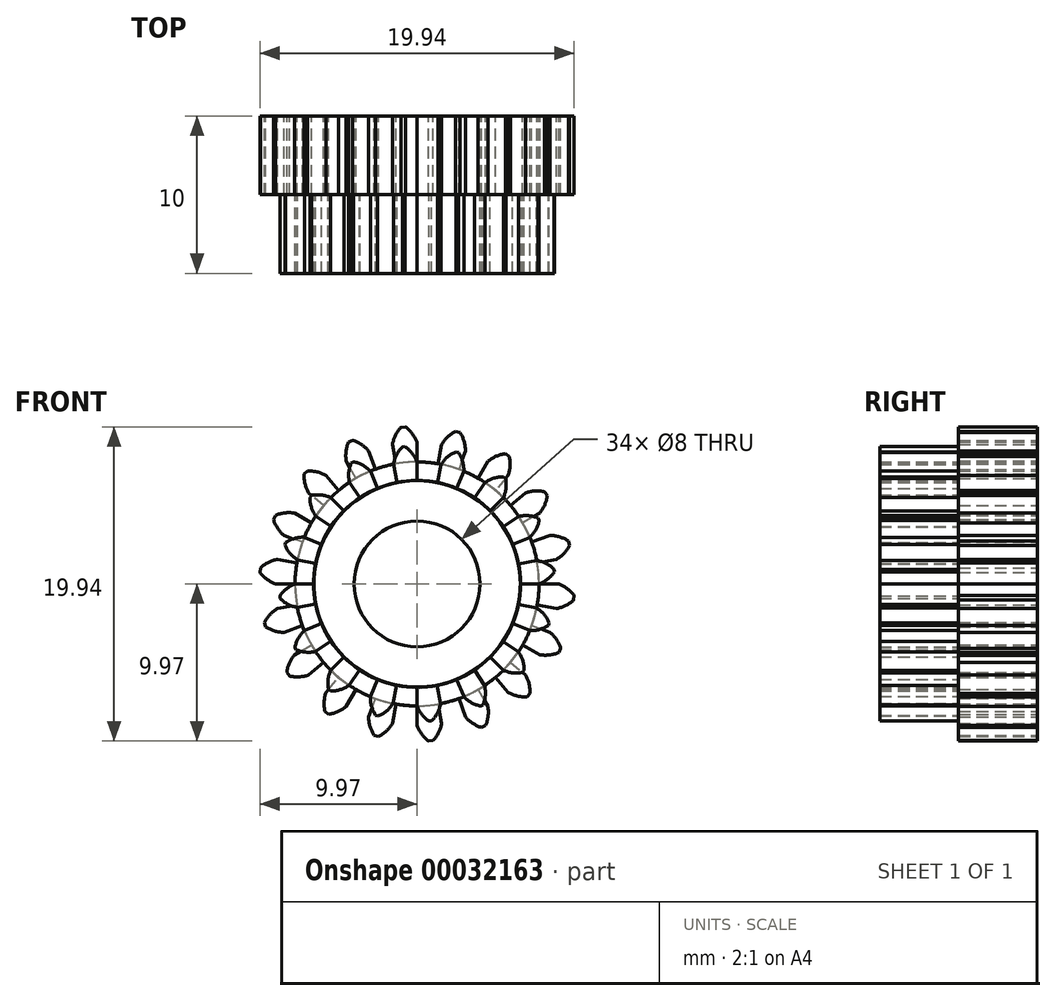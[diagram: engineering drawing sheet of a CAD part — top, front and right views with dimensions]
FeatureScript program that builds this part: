
annotation { "Feature Type Name" : "Feature", "Feature Type Description" : "" }
export const myFeature = defineFeature(function(context is Context, id is Id, definition is map)
    precondition{}
    {
        {
            var Q0;
            Q0=qCreatedBy(makeId("Front.planeOp"),FACE);
            var sketch = newSketch(context, id + "F0", { "sketchPlane" : qUnion([Q0])});
            skArc(sketch, "E0", {"start": v(0, 9) * mm, "mid": v(-0.3, 9.54) * mm, "end": v(-0.73, 9.97) * mm});
            skArc(sketch, "E1.0.MirrorCS", {"start": v(-1.56, 8.86) * mm, "mid": v(-1.36, 9.44) * mm, "end": v(-1.02, 9.95) * mm});
            skLineSegment(sketch, "E2.0.MirrorCS", {"start": v(-1.35, 7.63) * mm, "end": v(-1.56, 8.86) * mm});
            skLineSegment(sketch, "E3", {"start": v(-1.02, 9.95) * mm, "end": v(-0.73, 9.97) * mm});
            skPoint(sketch, "E4.orphan", {"position": v(-2.26, 12.8) * mm});
            skPoint(sketch, "E5.orphan", {"position": v(0, 13) * mm});
            skCircle(sketch, "E6", {"center": v(0, 0) * mm, "radius": 4 * mm});
            skArc(sketch, "E7", {"start": v(-1.35, 7.63) * mm, "mid": v(0.68, -7.72) * mm, "end": v(0, 7.75) * mm});
            skLineSegment(sketch, "E8", {"start": v(0, 9) * mm, "end": v(0, 7.75) * mm});
            skSolve(sketch);
        }
        {
            var Q0;
            Q0=makeQuery(id+"F0.imprint","IMPRINT",FACE,{"disambiguationData":[TD([[makeQuery(id+"F0.imprint","IMPRINT",EDGE,{"derivedFrom":sQuery(id+"F0.wireOp",EDGE,"E0")}),1.0]])]});
            extrude(context, id + "F1", {"entities" : qUnion([Q0]), "depth" : 5 * mm});
        }
        {
            var Q0;
            Q0=makeQuery(id+"F1.opExtrude","SWEPT_BODY",BODY,{"disambiguationData":[OSD([sQuery(id+"F0.wireOp",EDGE,"E0"),sQuery(id+"F0.wireOp",EDGE,"E1.0.MirrorCS"),sQuery(id+"F0.wireOp",EDGE,"E2.0.MirrorCS"),sQuery(id+"F0.wireOp",EDGE,"E3"),sQuery(id+"F0.wireOp",EDGE,"E6"),sQuery(id+"F0.wireOp",EDGE,"E7"),sQuery(id+"F0.wireOp",EDGE,"E8")])]});
            var Q1;
            Q1=makeQuery(id+"F1.opExtrude","SWEPT_FACE",FACE,{"disambiguationData":[OSD([sQuery(id+"F0.wireOp",EDGE,"E6")])]});
            circularPattern(context, id + "F2", {"entities" : qUnion([Q0]), "axis" : qUnion([Q1]), "angle" : 20 * degree, "instanceCount" : round(18)});
        }
        {
            var Q0;
            Q0=makeQuery(id+"F1.opExtrude","CAP_FACE",FACE,{"disambiguationData":[OSD([sQuery(id+"F0.wireOp",EDGE,"E0"),sQuery(id+"F0.wireOp",EDGE,"E1.0.MirrorCS"),sQuery(id+"F0.wireOp",EDGE,"E2.0.MirrorCS"),sQuery(id+"F0.wireOp",EDGE,"E3"),sQuery(id+"F0.wireOp",EDGE,"E6"),sQuery(id+"F0.wireOp",EDGE,"E7"),sQuery(id+"F0.wireOp",EDGE,"E8")])],"isStart":false});
            var sketch = newSketch(context, id + "F3", { "sketchPlane" : qUnion([Q0])});
            skLineSegment(sketch, "E9", {"start": v(0, 7.3) * mm, "end": v(0, 7.75) * mm});
            skArc(sketch, "E10.trimOffspring", {"start": v(0, 7.75) * mm, "mid": v(-0.3, 8.3) * mm, "end": v(-0.77, 8.72) * mm});
            skArc(sketch, "E11", {"start": v(-1.26, 6.44) * mm, "mid": v(0.63, -6.53) * mm, "end": v(0, 6.57) * mm});
            skLineSegment(sketch, "E12", {"start": v(0, 7.3) * mm, "end": v(0, 6.57) * mm});
            skCircle(sketch, "E13.0", {"center": v(0, 0) * mm, "radius": 4 * mm});
            skArc(sketch, "E14.0.MirrorCS", {"start": v(-1.5, 7.6) * mm, "mid": v(-1.3, 8.2) * mm, "end": v(-0.92, 8.7) * mm});
            skLineSegment(sketch, "E15.0.MirrorCS", {"start": v(-1.4, 7.17) * mm, "end": v(-1.5, 7.6) * mm});
            skLineSegment(sketch, "E16.0.MirrorCS", {"start": v(-1.4, 7.17) * mm, "end": v(-1.26, 6.44) * mm});
            skLineSegment(sketch, "E17", {"start": v(-0.77, 8.72) * mm, "end": v(-0.92, 8.7) * mm});
            skSolve(sketch);
        }
        {
            var Q0;
            Q0=makeQuery(id+"F3.imprint","IMPRINT",FACE,{"disambiguationData":[TD([[makeQuery(id+"F3.imprint","IMPRINT",EDGE,{"derivedFrom":sQuery(id+"F3.wireOp",EDGE,"E9")}),1.0]])]});
            var Q1;
            {var subQ0=makeQuery(id+"F1.opExtrude","CAP_EDGE",EDGE,{"disambiguationData":[OSD([sQuery(id+"F0.wireOp",EDGE,"E7")])],"isStart":false});var subQ3=makeQuery(id+"F1.opExtrude","CAP_EDGE",EDGE,{"disambiguationData":[OSD([sQuery(id+"F0.wireOp",EDGE,"E2.0.MirrorCS")])],"isStart":false});var subQ4=makeQuery(id+"F3.imprint","INTERSECT",VERTEX,{"derivedFrom":[subQ3,subQ0]});Q1=makeQuery(id+"F3.imprint","IMPRINT",FACE,{"disambiguationData":[TD([[makeQuery(id+"F3.imprint","IMPRINT",EDGE,{"disambiguationData":[TD([[subQ4,-1.0]])],"derivedFrom":subQ3}),1.0]])]});}
            extrude(context, id + "F4", {"entities" : qUnion([Q0, Q1]), "depth" : 5 * mm});
        }
        {
            var Q0;
            Q0=makeQuery(id+"F4.opExtrude","SWEPT_BODY",BODY,{"disambiguationData":[OSD([sQuery(id+"F3.wireOp",EDGE,"E9"),sQuery(id+"F3.wireOp",EDGE,"E10.trimOffspring"),sQuery(id+"F3.wireOp",EDGE,"E11"),sQuery(id+"F3.wireOp",EDGE,"E12"),sQuery(id+"F3.wireOp",EDGE,"E13.0"),sQuery(id+"F3.wireOp",EDGE,"E14.0.MirrorCS"),sQuery(id+"F3.wireOp",EDGE,"E15.0.MirrorCS"),sQuery(id+"F3.wireOp",EDGE,"E16.0.MirrorCS"),sQuery(id+"F3.wireOp",EDGE,"E17")])]});
            var Q1;
            Q1=makeQuery(id+"F1.opExtrude","SWEPT_FACE",FACE,{"disambiguationData":[OSD([sQuery(id+"F0.wireOp",EDGE,"E6")])]});
            circularPattern(context, id + "F5", {"entities" : qUnion([Q0]), "axis" : qUnion([Q1]), "angle" : 22.5 * degree, "instanceCount" : round(16)});
        }
    });
